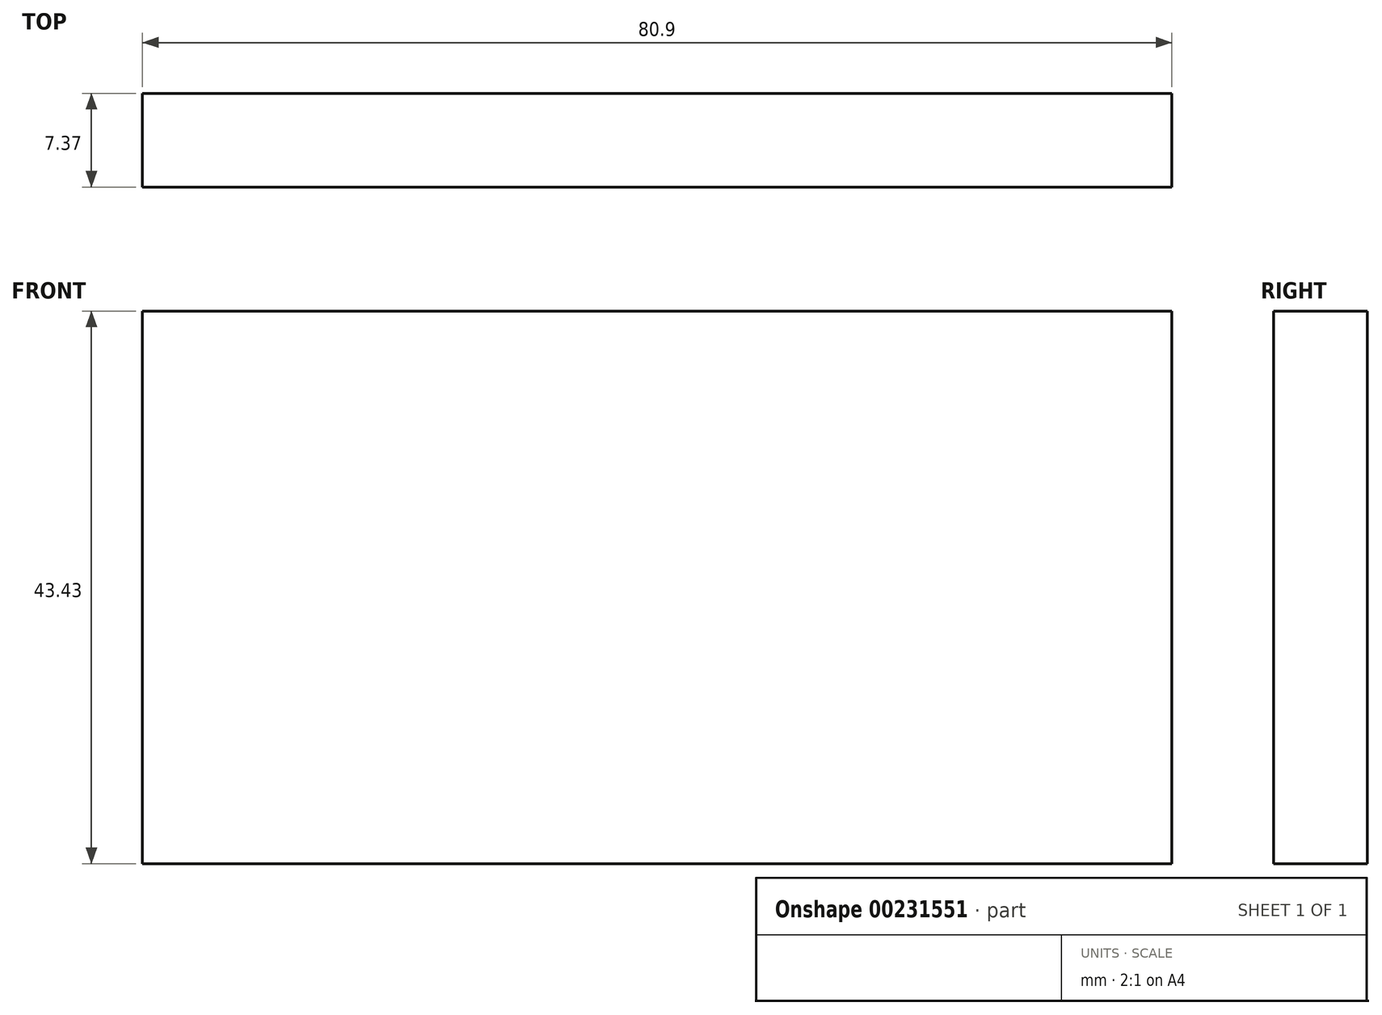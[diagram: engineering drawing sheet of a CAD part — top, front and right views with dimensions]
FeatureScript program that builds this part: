
annotation { "Feature Type Name" : "Feature", "Feature Type Description" : "" }
export const myFeature = defineFeature(function(context is Context, id is Id, definition is map)
    precondition{}
    {
        {
            var Q0;
            Q0=qCreatedBy(makeId("Front.planeOp"),FACE);
            var sketch = newSketch(context, id + "F0", { "sketchPlane" : qUnion([Q0])});
            skLineSegment(sketch, "E0.bottom", {"start": v(-39.46, 21.12) * mm, "end": v(41.44, 21.12) * mm});
            skLineSegment(sketch, "E0.top", {"start": v(-39.46, -22.3) * mm, "end": v(41.44, -22.3) * mm});
            skLineSegment(sketch, "E0.left", {"start": v(-39.46, 21.12) * mm, "end": v(-39.46, -22.3) * mm});
            skLineSegment(sketch, "E0.right", {"start": v(41.44, 21.12) * mm, "end": v(41.44, -22.3) * mm});
            skSolve(sketch);
        }
        {
            var Q0;
            Q0 = qSketchRegion(id + "F0", true);
            extrude(context, id + "F1", {"entities" : qUnion([Q0]), "depth" : 7.37 * mm});
        }
    });
